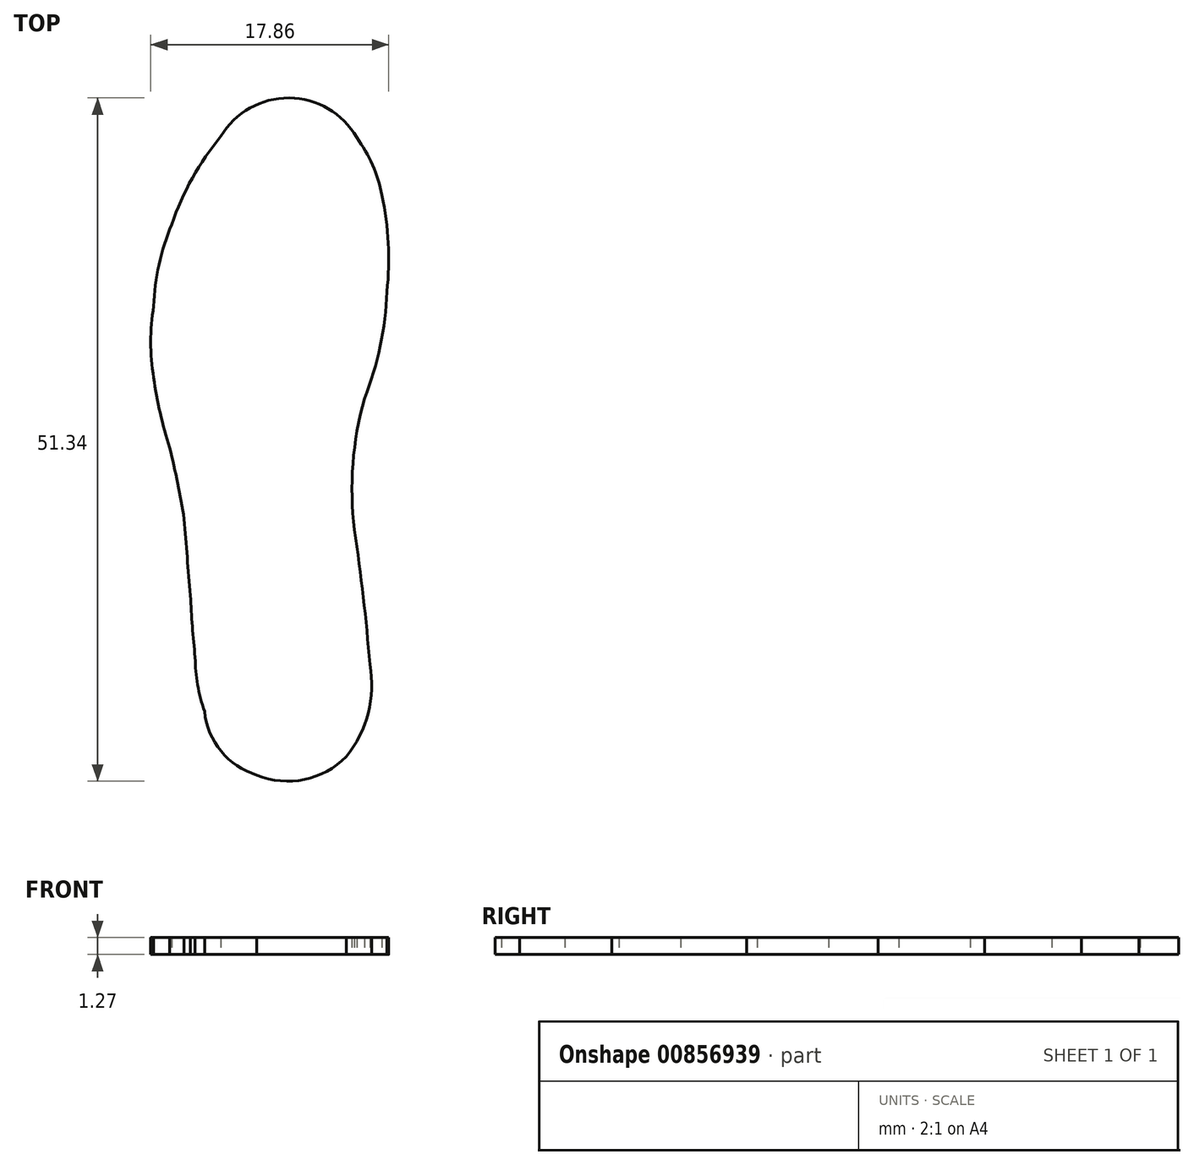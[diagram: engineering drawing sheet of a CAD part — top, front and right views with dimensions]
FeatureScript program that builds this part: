
annotation { "Feature Type Name" : "Feature", "Feature Type Description" : "" }
export const myFeature = defineFeature(function(context is Context, id is Id, definition is map)
    precondition{}
    {
        {
            var Q0;
            Q0=qCreatedBy(makeId("Top.planeOp"),FACE);
            var sketch = newSketch(context, id + "F0", { "sketchPlane" : qUnion([Q0])});
            skArc(sketch, "E0", {"start": v(-4.77, 21.55) * mm, "mid": v(-9.85, 24.53) * mm, "end": v(-14.98, 21.64) * mm});
            skArc(sketch, "E1", {"start": v(-14.98, 21.64) * mm, "mid": v(-17.13, 18.5) * mm, "end": v(-18.66, 15.02) * mm});
            skArc(sketch, "E2", {"start": v(-18.66, 15.02) * mm, "mid": v(-19.63, 12.01) * mm, "end": v(-20.03, 8.87) * mm});
            skArc(sketch, "E3", {"start": v(-20.03, 8.87) * mm, "mid": v(-20.24, 6.2) * mm, "end": v(-20.03, 3.5) * mm});
            skArc(sketch, "E4", {"start": v(-20.03, 3.5) * mm, "mid": v(-19.54, 0.85) * mm, "end": v(-18.82, -1.76) * mm});
            skArc(sketch, "E5", {"start": v(-17.73, -7.11) * mm, "mid": v(-18.22, -4.42) * mm, "end": v(-18.82, -1.76) * mm});
            skArc(sketch, "E6", {"start": v(-17.73, -7.11) * mm, "mid": v(-17.5, -9.99) * mm, "end": v(-17.26, -12.86) * mm});
            skArc(sketch, "E7", {"start": v(-17.26, -12.86) * mm, "mid": v(-17.12, -15.19) * mm, "end": v(-16.9, -17.5) * mm});
            skArc(sketch, "E8", {"start": v(-16.9, -17.5) * mm, "mid": v(-16.72, -19.57) * mm, "end": v(-16.2, -21.58) * mm});
            skArc(sketch, "E9", {"start": v(-16.2, -21.58) * mm, "mid": v(-14.96, -24.55) * mm, "end": v(-12.28, -26.34) * mm});
            skArc(sketch, "E10", {"start": v(-12.28, -26.34) * mm, "mid": v(-8.7, -26.68) * mm, "end": v(-5.56, -24.96) * mm});
            skArc(sketch, "E11", {"start": v(-5.56, -24.96) * mm, "mid": v(-3.92, -21.7) * mm, "end": v(-3.8, -18.05) * mm});
            skArc(sketch, "E12", {"start": v(-3.8, -18.05) * mm, "mid": v(-4.28, -12.97) * mm, "end": v(-4.95, -7.92) * mm});
            skArc(sketch, "E13", {"start": v(-4.2, 1.94) * mm, "mid": v(-5.06, -2.95) * mm, "end": v(-4.95, -7.92) * mm});
            skArc(sketch, "E14", {"start": v(-4.2, 1.94) * mm, "mid": v(-3.01, 5.89) * mm, "end": v(-2.5, 9.97) * mm});
            skArc(sketch, "E15", {"start": v(-2.5, 9.97) * mm, "mid": v(-2.4, 13.61) * mm, "end": v(-2.88, 17.22) * mm});
            skArc(sketch, "E16", {"start": v(-2.88, 17.22) * mm, "mid": v(-3.6, 19.49) * mm, "end": v(-4.77, 21.55) * mm});
            skSolve(sketch);
        }
        {
            var Q0;
            Q0 = qSketchRegion(id + "F0", true);
            extrude(context, id + "F1", {"entities" : qUnion([Q0]), "depth" : 1.27 * mm, "offsetDistance" : 25.4 * mm});
        }
    });
